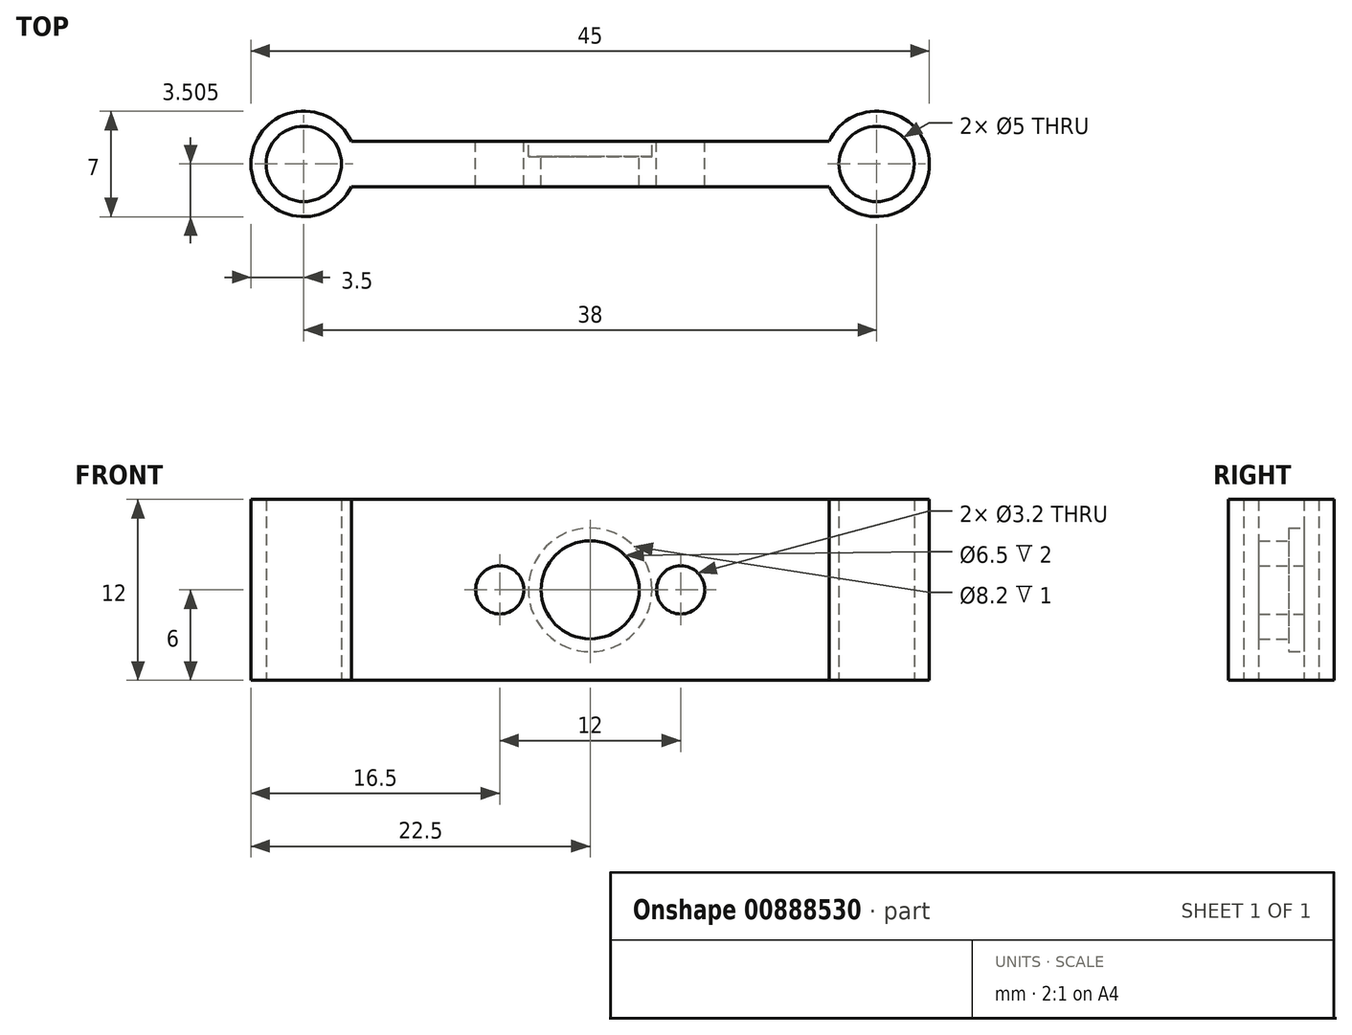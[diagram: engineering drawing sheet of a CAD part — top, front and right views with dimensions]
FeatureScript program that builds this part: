
annotation { "Feature Type Name" : "Feature", "Feature Type Description" : "" }
export const myFeature = defineFeature(function(context is Context, id is Id, definition is map)
    precondition{}
    {
        {
            var Q0;
            Q0=qCreatedBy(makeId("Top.planeOp"),FACE);
            var sketch = newSketch(context, id + "F0", { "sketchPlane" : qUnion([Q0])});
            skLineSegment(sketch, "E0.bottom", {"start": v(-19, 1.12) * mm, "end": v(19, 1.12) * mm});
            skLineSegment(sketch, "E0.top", {"start": v(-19, -1.88) * mm, "end": v(19, -1.88) * mm});
            skLineSegment(sketch, "E0.left", {"start": v(-19, 1.12) * mm, "end": v(-19, -1.88) * mm});
            skLineSegment(sketch, "E0.right", {"start": v(19, 1.12) * mm, "end": v(19, -1.88) * mm});
            skPoint(sketch, "E1", {"position": v(-19, -0.38) * mm});
            skCircle(sketch, "E2", {"center": v(-19, -0.38) * mm, "radius": 3.5 * mm});
            skCircle(sketch, "E3", {"center": v(19, -0.38) * mm, "radius": 3.5 * mm});
            skSolve(sketch);
        }
        {
            var Q0;
            Q0 = qSketchRegion(id + "F0", true);
            extrude(context, id + "F1", {"entities" : qUnion([Q0]), "depth" : 12 * mm, "offsetDistance" : 25 * mm});
        }
        {
            var Q0;
            Q0=sQuery(id+"F0.wireOp",VERTEX,"35dba5de-8aa0-4c4d-8b60-120a7edc57c8");
            var Q1;
            Q1=sQuery(id+"F0.wireOp",VERTEX,"E3.center");
            var Q2;
            Q2=makeQuery(id+"F1.opExtrude","SWEPT_BODY",BODY,{"disambiguationData":[OSD([sQuery(id+"F0.wireOp",EDGE,"E0.bottom"),sQuery(id+"F0.wireOp",EDGE,"E0.top"),sQuery(id+"F0.wireOp",EDGE,"E2"),sQuery(id+"F0.wireOp",EDGE,"E3")])]});
            hole(context, id + "F2", {"style" : HoleStyle.SIMPLE, "endStyle" : HoleEndStyle.BLIND, "oppositeDirection" : true, "holeDiameter" : 5 * mm, "majorDiameter" : 5 * mm, "holeDepth" : 15 * mm, "isTappedThrough" : true, "tappedDepth" : 12 * mm, "tapClearance" : 3, "locations" : qUnion([Q0, Q1]), "scope" : qUnion([Q2])});
        }
        {
            var Q0;
            Q0=sQuery(id+"F0.wireOp",VERTEX,"E1");
            var Q1;
            Q1=makeQuery(id+"F1.opExtrude","SWEPT_BODY",BODY,{"disambiguationData":[OSD([sQuery(id+"F0.wireOp",EDGE,"E0.bottom"),sQuery(id+"F0.wireOp",EDGE,"E0.top"),sQuery(id+"F0.wireOp",EDGE,"E2"),sQuery(id+"F0.wireOp",EDGE,"E3")])]});
            hole(context, id + "F3", {"style" : HoleStyle.SIMPLE, "endStyle" : HoleEndStyle.BLIND, "oppositeDirection" : true, "holeDiameter" : 5 * mm, "majorDiameter" : 5 * mm, "holeDepth" : 15 * mm, "isTappedThrough" : true, "tappedDepth" : 12 * mm, "tapClearance" : 3, "locations" : qUnion([Q0]), "scope" : qUnion([Q1])});
        }
        {
            var Q0;
            Q0=makeQuery(id+"F1.opExtrude","SWEPT_FACE",FACE,{"disambiguationData":[OSD([sQuery(id+"F0.wireOp",EDGE,"E0.bottom")])]});
            var sketch = newSketch(context, id + "F4", { "sketchPlane" : qUnion([Q0])});
            skPoint(sketch, "E4", {"position": v(0, 6) * mm});
            skPoint(sketch, "E4.positionSnap0", {"position": v(0, 12) * mm});
            skPoint(sketch, "E5", {"position": v(-6, 6) * mm});
            skPoint(sketch, "E6", {"position": v(6, 6) * mm});
            skSolve(sketch);
        }
        {
            var Q0;
            Q0=sQuery(id+"F4.wireOp",VERTEX,"E4");
            var Q1;
            Q1=makeQuery(id+"F1.opExtrude","SWEPT_BODY",BODY,{"disambiguationData":[OSD([sQuery(id+"F0.wireOp",EDGE,"E0.bottom"),sQuery(id+"F0.wireOp",EDGE,"E0.top"),sQuery(id+"F0.wireOp",EDGE,"E2"),sQuery(id+"F0.wireOp",EDGE,"E3")])]});
            hole(context, id + "F5", {"style" : HoleStyle.C_BORE, "endStyle" : HoleEndStyle.BLIND, "holeDiameter" : 6.5 * mm, "cBoreDiameter" : 8.2 * mm, "cBoreDepth" : 1 * mm, "majorDiameter" : 5 * mm, "holeDepth" : 10 * mm, "isTappedThrough" : true, "tappedDepth" : 12 * mm, "tapClearance" : 3, "locations" : qUnion([Q0]), "scope" : qUnion([Q1])});
        }
        {
            var Q0;
            Q0=sQuery(id+"F4.wireOp",VERTEX,"E5");
            var Q1;
            Q1=makeQuery(id+"F1.opExtrude","SWEPT_BODY",BODY,{"disambiguationData":[OSD([sQuery(id+"F0.wireOp",EDGE,"E0.bottom"),sQuery(id+"F0.wireOp",EDGE,"E0.top"),sQuery(id+"F0.wireOp",EDGE,"E2"),sQuery(id+"F0.wireOp",EDGE,"E3")])]});
            hole(context, id + "F6", {"style" : HoleStyle.SIMPLE, "endStyle" : HoleEndStyle.BLIND, "holeDiameter" : 3.2 * mm, "majorDiameter" : 5 * mm, "holeDepth" : 15 * mm, "isTappedThrough" : true, "tappedDepth" : 12 * mm, "tapClearance" : 3, "locations" : qUnion([Q0]), "scope" : qUnion([Q1])});
        }
        {
            var Q0;
            Q0=sQuery(id+"F4.wireOp",VERTEX,"E6");
            var Q1;
            Q1=makeQuery(id+"F1.opExtrude","SWEPT_BODY",BODY,{"disambiguationData":[OSD([sQuery(id+"F0.wireOp",EDGE,"E0.bottom"),sQuery(id+"F0.wireOp",EDGE,"E0.top"),sQuery(id+"F0.wireOp",EDGE,"E2"),sQuery(id+"F0.wireOp",EDGE,"E3")])]});
            hole(context, id + "F7", {"style" : HoleStyle.SIMPLE, "endStyle" : HoleEndStyle.BLIND, "holeDiameter" : 3.2 * mm, "majorDiameter" : 5 * mm, "holeDepth" : 15 * mm, "isTappedThrough" : true, "tappedDepth" : 12 * mm, "tapClearance" : 3, "locations" : qUnion([Q0]), "scope" : qUnion([Q1])});
        }
    });
